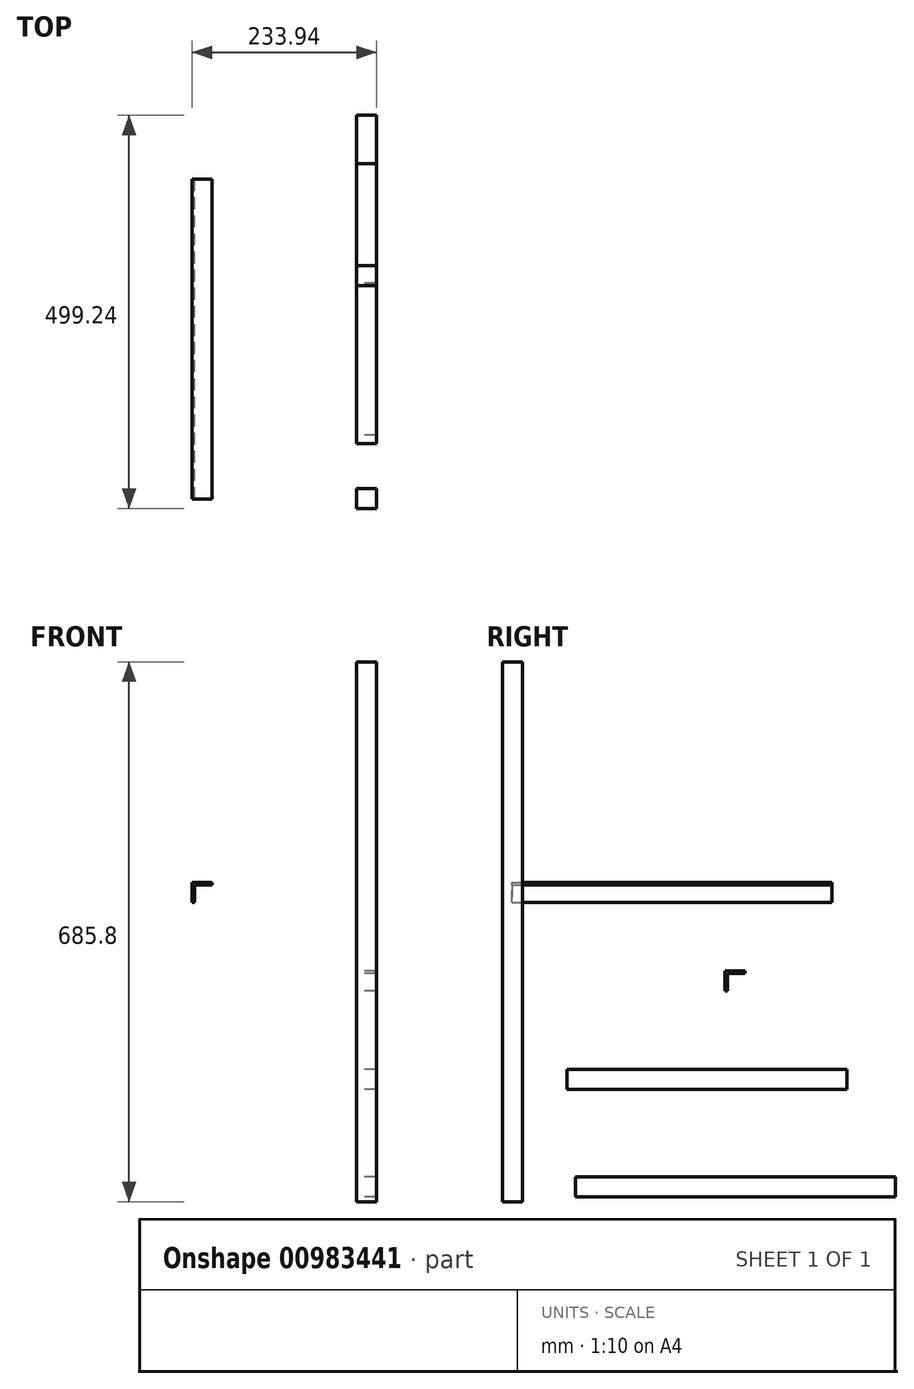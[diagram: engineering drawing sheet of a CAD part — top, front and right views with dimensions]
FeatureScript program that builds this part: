
annotation { "Feature Type Name" : "Feature", "Feature Type Description" : "" }
export const myFeature = defineFeature(function(context is Context, id is Id, definition is map)
    precondition{}
    {
        {
            var Q0;
            Q0=qCreatedBy(makeId("Right.planeOp"),FACE);
            var sketch = newSketch(context, id + "F0", { "sketchPlane" : qUnion([Q0])});
            skLineSegment(sketch, "E0.bottom", {"start": v(-418.48, 344.27) * mm, "end": v(-393.08, 344.27) * mm});
            skLineSegment(sketch, "E0.top", {"start": v(-418.48, -341.53) * mm, "end": v(-393.08, -341.53) * mm});
            skLineSegment(sketch, "E0.left", {"start": v(-418.48, 344.27) * mm, "end": v(-418.48, -341.53) * mm});
            skLineSegment(sketch, "E0.right", {"start": v(-393.08, 344.27) * mm, "end": v(-393.08, -341.53) * mm});
            skLineSegment(sketch, "E1.bottom", {"start": v(-325.64, -335.2) * mm, "end": v(80.76, -335.2) * mm});
            skLineSegment(sketch, "E1.top", {"start": v(-325.64, -309.8) * mm, "end": v(80.76, -309.8) * mm});
            skLineSegment(sketch, "E1.left", {"start": v(-325.64, -335.2) * mm, "end": v(-325.64, -309.8) * mm});
            skLineSegment(sketch, "E1.right", {"start": v(80.76, -335.2) * mm, "end": v(80.76, -309.8) * mm});
            skLineSegment(sketch, "E2.bottom", {"start": v(-336.05, -199.02) * mm, "end": v(19.55, -199.02) * mm});
            skLineSegment(sketch, "E2.top", {"start": v(-336.05, -173.62) * mm, "end": v(19.55, -173.62) * mm});
            skLineSegment(sketch, "E2.left", {"start": v(-336.05, -199.02) * mm, "end": v(-336.05, -173.62) * mm});
            skLineSegment(sketch, "E2.right", {"start": v(19.55, -199.02) * mm, "end": v(19.55, -173.62) * mm});
            skSolve(sketch);
        }
        {
            var Q0;
            Q0=qCreatedBy(makeId("Front.planeOp"),FACE);
            var sketch = newSketch(context, id + "F1", { "sketchPlane" : qUnion([Q0])});
            skLineSegment(sketch, "E3", {"start": v(-208.54, 38.63) * mm, "end": v(-208.54, 64.03) * mm});
            skLineSegment(sketch, "E4", {"start": v(-208.54, 64.03) * mm, "end": v(-183.14, 64.03) * mm});
            skLineSegment(sketch, "E5", {"start": v(-183.14, 64.03) * mm, "end": v(-183.14, 60.86) * mm});
            skLineSegment(sketch, "E6", {"start": v(-183.14, 60.86) * mm, "end": v(-205.37, 60.86) * mm});
            skLineSegment(sketch, "E7", {"start": v(-205.37, 60.86) * mm, "end": v(-205.37, 38.63) * mm});
            skLineSegment(sketch, "E8", {"start": v(-205.37, 38.63) * mm, "end": v(-208.54, 38.63) * mm});
            skSolve(sketch);
        }
        {
            var Q0;
            Q0=makeQuery(id+"F0.imprint","IMPRINT",FACE,{"disambiguationData":[TD([[makeQuery(id+"F0.imprint","IMPRINT",EDGE,{"derivedFrom":sQuery(id+"F0.wireOp",EDGE,"E0.bottom")}),-1.0]])]});
            var Q1;
            Q1=makeQuery(id+"F0.imprint","IMPRINT",FACE,{"disambiguationData":[TD([[makeQuery(id+"F0.imprint","IMPRINT",EDGE,{"derivedFrom":sQuery(id+"F0.wireOp",EDGE,"E1.bottom")}),1.0]])]});
            var Q2;
            Q2=makeQuery(id+"F0.imprint","IMPRINT",FACE,{"disambiguationData":[TD([[makeQuery(id+"F0.imprint","IMPRINT",EDGE,{"derivedFrom":sQuery(id+"F0.wireOp",EDGE,"E2.bottom")}),1.0]])]});
            extrude(context, id + "F2", {"entities" : qUnion([Q0, Q1, Q2]), "depth" : 25.4 * mm, "offsetDistance" : 25.4 * mm});
        }
        {
            var Q0;
            Q0=makeQuery(id+"F1.imprint","IMPRINT",FACE,{"disambiguationData":[TD([[makeQuery(id+"F1.imprint","IMPRINT",EDGE,{"derivedFrom":sQuery(id+"F1.wireOp",EDGE,"E3")}),-1.0]])]});
            extrude(context, id + "F3", {"entities" : qUnion([Q0]), "depth" : 406.4 * mm, "offsetDistance" : 25.4 * mm});
        }
        {
            var Q0;
            Q0=qCreatedBy(makeId("Right.planeOp"),FACE);
            var sketch = newSketch(context, id + "F4", { "sketchPlane" : qUnion([Q0])});
            skLineSegment(sketch, "E9", {"start": v(-135.51, -73.93) * mm, "end": v(-135.51, -48.53) * mm});
            skLineSegment(sketch, "E10", {"start": v(-135.51, -48.53) * mm, "end": v(-110.11, -48.53) * mm});
            skLineSegment(sketch, "E11", {"start": v(-110.11, -48.53) * mm, "end": v(-110.11, -51.7) * mm});
            skLineSegment(sketch, "E12", {"start": v(-110.11, -51.7) * mm, "end": v(-132.34, -51.7) * mm});
            skLineSegment(sketch, "E13", {"start": v(-132.34, -51.7) * mm, "end": v(-132.34, -73.93) * mm});
            skLineSegment(sketch, "E14", {"start": v(-132.34, -73.93) * mm, "end": v(-135.51, -73.93) * mm});
            skSolve(sketch);
        }
        {
            var Q0;
            Q0=makeQuery(id+"F4.imprint","IMPRINT",FACE,{"disambiguationData":[TD([[makeQuery(id+"F4.imprint","IMPRINT",EDGE,{"derivedFrom":sQuery(id+"F4.wireOp",EDGE,"E9")}),-1.0]])]});
            extrude(context, id + "F5", {"entities" : qUnion([Q0]), "depth" : 25.4 * mm, "offsetDistance" : 25.4 * mm});
        }
    });
